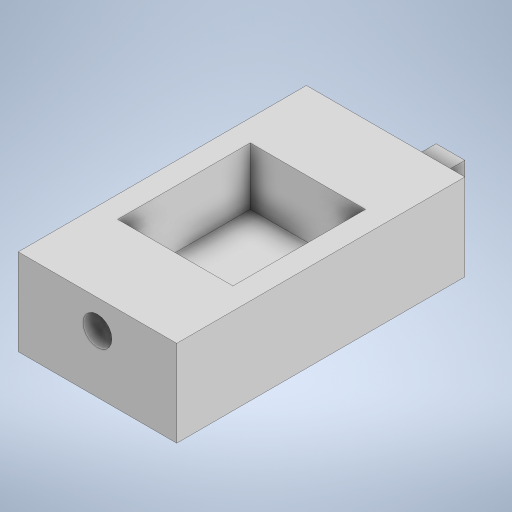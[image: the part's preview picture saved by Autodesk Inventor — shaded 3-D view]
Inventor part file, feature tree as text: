
AUTODESK INVENTOR PART (.ipt)
format: ipt  version: 2023 (Build 270158000, 158)  size: 233,472 bytes
history: native  units: mm
features: extrude x4, sketch x4, other x1
ambient origin geometry x8: Origin, YZ Plane, XZ Plane, XY Plane, X Axis, Y Axis, Z Axis, Center Point
bodies: Body1 (feature_tree)
feature tree (9):
  other  "Sólido1"
  extrude  "Extrusión1"  Depth=100.0mm
  extrude  "Extrusión2"  Depth=10.0mm
  extrude  "Extrusión3"  Depth=5.0mm
  extrude  "Extrusión4"  Depth=10.0mm TaperAngle=0.0deg
  sketch  "Boceto1"  dims[d0=55.0mm d1=100.0mm]
  sketch  "Boceto2"  dims[d2=30.0mm d3=0.0mm d4=10.0mm]
  sketch  "Boceto3"  dims[d5=10.0mm d6=5.0mm]
  sketch  "Boceto4"  dims[d7=10.0mm d8=10.0mm d9=0.0mm d10=10.0mm d11=10.0mm d12=15.0mm d13=0.0mm d14=40.0mm d15=46.0mm d16=20.0mm d17=0.0mm]
